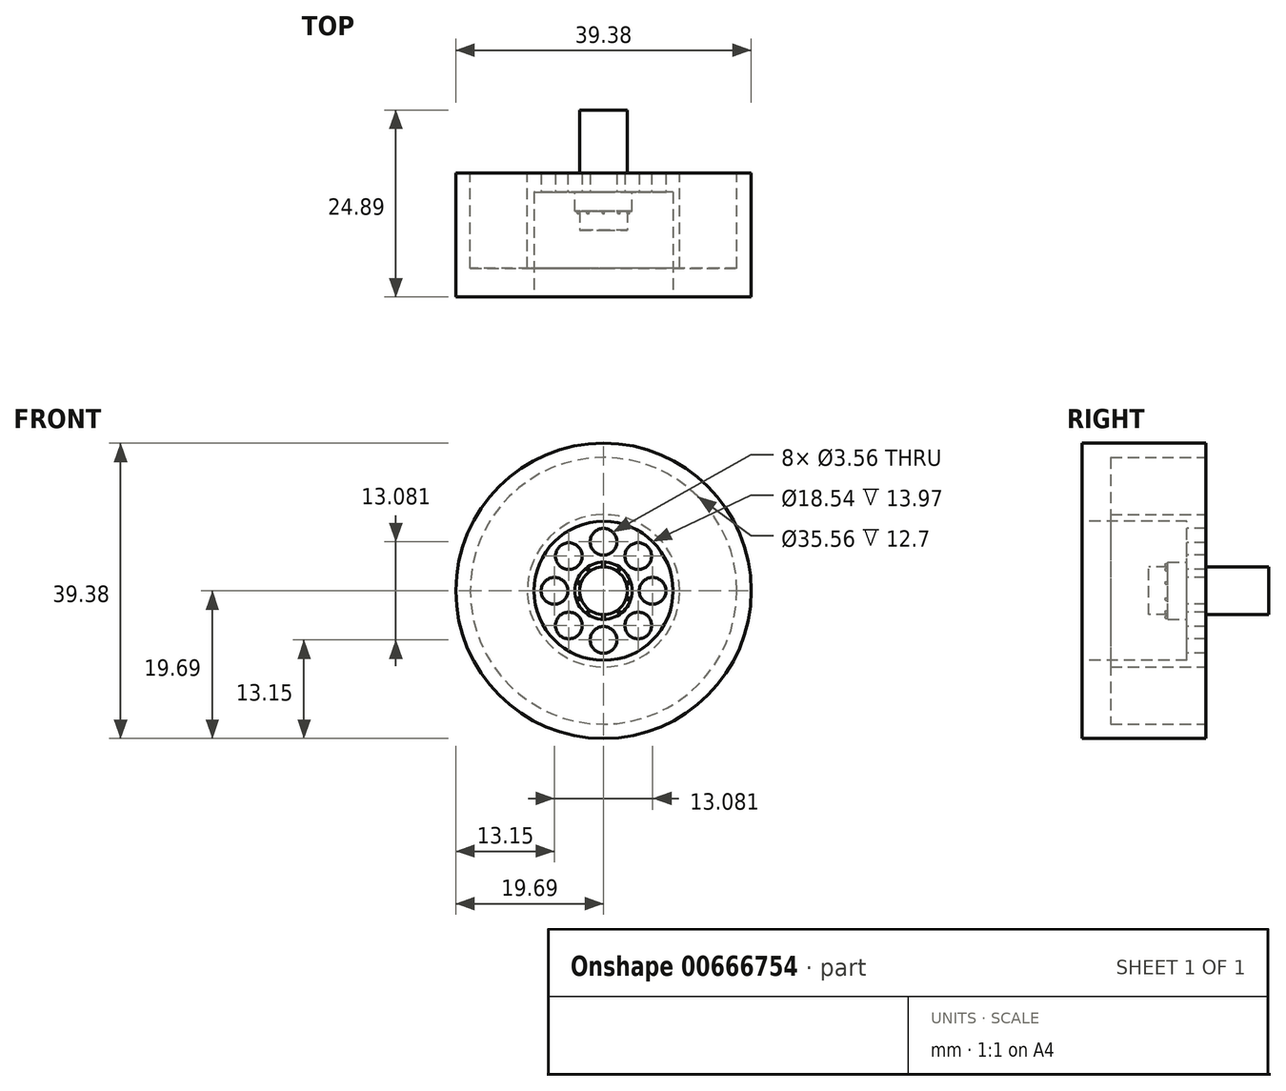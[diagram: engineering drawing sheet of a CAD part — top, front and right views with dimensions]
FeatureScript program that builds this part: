
annotation { "Feature Type Name" : "Feature", "Feature Type Description" : "" }
export const myFeature = defineFeature(function(context is Context, id is Id, definition is map)
    precondition{}
    {
        {
            var Q0;
            Q0=qCreatedBy(makeId("Front.planeOp"),FACE);
            var sketch = newSketch(context, id + "F0", { "sketchPlane" : qUnion([Q0])});
            skCircle(sketch, "E0", {"center": v(0, 0) * mm, "radius": 19.69 * mm});
            skCircle(sketch, "E1", {"center": v(0, 0) * mm, "radius": 8.9 * mm});
            skCircle(sketch, "E2", {"center": v(0, 0) * mm, "radius": 10.16 * mm});
            skSolve(sketch);
        }
        {
            var Q0;
            Q0=makeQuery(id+"F0.imprint","IMPRINT",FACE,{"disambiguationData":[TD([[makeQuery(id+"F0.imprint","IMPRINT",EDGE,{"derivedFrom":sQuery(id+"F0.wireOp",EDGE,"E0")}),1.0]])]});
            var Q1;
            Q1=makeQuery(id+"F0.imprint","IMPRINT",FACE,{"disambiguationData":[TD([[makeQuery(id+"F0.imprint","IMPRINT",EDGE,{"derivedFrom":sQuery(id+"F0.wireOp",EDGE,"E1")}),-1.0]])]});
            var Q2;
            Q2=makeQuery(id+"F0.imprint","IMPRINT",FACE,{"disambiguationData":[TD([[makeQuery(id+"F0.imprint","IMPRINT",EDGE,{"derivedFrom":sQuery(id+"F0.wireOp",EDGE,"E1")}),1.0]])]});
            extrude(context, id + "F1", {"entities" : qUnion([Q0, Q1, Q2]), "depth" : 24.9 * mm, "offsetDistance" : 25.4 * mm});
        }
        {
            var Q0;
            Q0=makeQuery(id+"F1.opExtrude","CAP_FACE",FACE,{"disambiguationData":[OSD([sQuery(id+"F0.wireOp",EDGE,"E0")])],"isStart":true});
            var sketch = newSketch(context, id + "F2", { "sketchPlane" : qUnion([Q0])});
            skCircle(sketch, "E3", {"center": v(0, 0) * mm, "radius": 3.18 * mm});
            skSolve(sketch);
        }
        {
            var Q0;
            Q0=makeQuery(id+"F2.imprint","IMPRINT",FACE,{"disambiguationData":[TD([[makeQuery(id+"F2.imprint","IMPRINT",EDGE,{"derivedFrom":sQuery(id+"F2.wireOp",EDGE,"E3")}),-1.0]])]});
            extrude(context, id + "F3", {"entities" : qUnion([Q0]), "operationType" : NewBodyOperationType.REMOVE, "oppositeDirection" : true, "depth" : 8.38 * mm, "offsetDistance" : 25.4 * mm});
        }
        {
            var Q0;
            Q0=makeQuery(id+"F1.opExtrude","CAP_FACE",FACE,{"disambiguationData":[OSD([sQuery(id+"F0.wireOp",EDGE,"E0")])],"isStart":false});
            var sketch = newSketch(context, id + "F4", { "sketchPlane" : qUnion([Q0])});
            skCircle(sketch, "E4", {"center": v(0, 0) * mm, "radius": 9.27 * mm});
            skSolve(sketch);
        }
        {
            var Q0;
            Q0=makeQuery(id+"F4.imprint","IMPRINT",FACE,{"disambiguationData":[TD([[makeQuery(id+"F4.imprint","IMPRINT",EDGE,{"derivedFrom":sQuery(id+"F4.wireOp",EDGE,"E4")}),1.0]])]});
            extrude(context, id + "F5", {"entities" : qUnion([Q0]), "operationType" : NewBodyOperationType.REMOVE, "oppositeDirection" : true, "depth" : 8.9 * mm, "offsetDistance" : 25.4 * mm});
        }
        {
            var Q0;
            Q0=makeQuery(id+"F5.boolean.opBoolean","COPY",FACE,{"derivedFrom":makeQuery(id+"F5.opExtrude","CAP_FACE",FACE,{"disambiguationData":[OSD([sQuery(id+"F4.wireOp",EDGE,"E4")])],"isStart":false})});
            var sketch = newSketch(context, id + "F6", { "sketchPlane" : qUnion([Q0])});
            skCircle(sketch, "E5", {"center": v(0, 0) * mm, "radius": 3.18 * mm});
            skSolve(sketch);
        }
        {
            var Q0;
            Q0=makeQuery(id+"F6.imprint","IMPRINT",FACE,{"disambiguationData":[TD([[makeQuery(id+"F6.imprint","IMPRINT",EDGE,{"derivedFrom":sQuery(id+"F6.wireOp",EDGE,"E5")}),-1.0]])]});
            extrude(context, id + "F7", {"entities" : qUnion([Q0]), "operationType" : NewBodyOperationType.REMOVE, "oppositeDirection" : true, "depth" : 5.08 * mm, "offsetDistance" : 25.4 * mm});
        }
        {
            var Q0;
            Q0=makeQuery(id+"F7.boolean.opBoolean","COPY",FACE,{"derivedFrom":makeQuery(id+"F7.opExtrude","CAP_FACE",FACE,{"disambiguationData":[OSD([sQuery(id+"F4.wireOp",EDGE,"E4"),sQuery(id+"F6.wireOp",EDGE,"E5")])],"isStart":false})});
            var sketch = newSketch(context, id + "F8", { "sketchPlane" : qUnion([Q0])});
            skCircle(sketch, "E6", {"center": v(0, 0) * mm, "radius": 3.81 * mm});
            skSolve(sketch);
        }
        {
            var Q0;
            Q0=makeQuery(id+"F8.imprint","IMPRINT",FACE,{"disambiguationData":[TD([[makeQuery(id+"F8.imprint","IMPRINT",EDGE,{"derivedFrom":sQuery(id+"F8.wireOp",EDGE,"E6")}),1.0]])]});
            extrude(context, id + "F9", {"entities" : qUnion([Q0]), "operationType" : NewBodyOperationType.ADD, "depth" : 2.54 * mm, "offsetDistance" : 25.4 * mm});
        }
        {
            var Q0;
            Q0=makeQuery(id+"F7.boolean.opBoolean","COPY",FACE,{"derivedFrom":makeQuery(id+"F7.opExtrude","CAP_FACE",FACE,{"disambiguationData":[OSD([sQuery(id+"F4.wireOp",EDGE,"E4"),sQuery(id+"F6.wireOp",EDGE,"E5")])],"isStart":false})});
            var sketch = newSketch(context, id + "F10", { "sketchPlane" : qUnion([Q0])});
            skLineSegment(sketch, "E7", {"start": v(0, 3.81) * mm, "end": v(0, 6.54) * mm});
            skCircle(sketch, "E8", {"center": v(0, 6.54) * mm, "radius": 1.78 * mm});
            skCircle(sketch, "E9.1.0", {"center": v(-4.62, 4.62) * mm, "radius": 1.78 * mm});
            skCircle(sketch, "E9.2.0", {"center": v(-6.54, 0) * mm, "radius": 1.78 * mm});
            skPoint(sketch, "E9.center", {"position": v(0, 0) * mm});
            skCircle(sketch, "E10.1.3.0", {"center": v(-4.62, -4.62) * mm, "radius": 1.78 * mm});
            skCircle(sketch, "E10.1.4.0", {"center": v(0, -6.54) * mm, "radius": 1.78 * mm});
            skCircle(sketch, "E10.1.5.0", {"center": v(4.62, -4.62) * mm, "radius": 1.78 * mm});
            skCircle(sketch, "E10.1.6.0", {"center": v(6.54, 0) * mm, "radius": 1.78 * mm});
            skCircle(sketch, "E10.1.7.0", {"center": v(4.62, 4.62) * mm, "radius": 1.78 * mm});
            skSolve(sketch);
        }
        {
            var Q0;
            Q0=makeQuery(id+"F10.imprint","IMPRINT",FACE,{"disambiguationData":[TD([[makeQuery(id+"F10.imprint","IMPRINT",EDGE,{"derivedFrom":sQuery(id+"F10.wireOp",EDGE,"E9.1.0")}),1.0]])]});
            var Q1;
            Q1=makeQuery(id+"F10.imprint","IMPRINT",FACE,{"disambiguationData":[TD([[makeQuery(id+"F10.imprint","IMPRINT",EDGE,{"derivedFrom":sQuery(id+"F10.wireOp",EDGE,"E8")}),1.0]])]});
            var Q2;
            Q2=makeQuery(id+"F10.imprint","IMPRINT",FACE,{"disambiguationData":[TD([[makeQuery(id+"F10.imprint","IMPRINT",EDGE,{"derivedFrom":sQuery(id+"F10.wireOp",EDGE,"E10.1.7.0")}),1.0]])]});
            var Q3;
            Q3=makeQuery(id+"F10.imprint","IMPRINT",FACE,{"disambiguationData":[TD([[makeQuery(id+"F10.imprint","IMPRINT",EDGE,{"derivedFrom":sQuery(id+"F10.wireOp",EDGE,"E10.1.6.0")}),1.0]])]});
            var Q4;
            Q4=makeQuery(id+"F10.imprint","IMPRINT",FACE,{"disambiguationData":[TD([[makeQuery(id+"F10.imprint","IMPRINT",EDGE,{"derivedFrom":sQuery(id+"F10.wireOp",EDGE,"E10.1.5.0")}),1.0]])]});
            var Q5;
            Q5=makeQuery(id+"F10.imprint","IMPRINT",FACE,{"disambiguationData":[TD([[makeQuery(id+"F10.imprint","IMPRINT",EDGE,{"derivedFrom":sQuery(id+"F10.wireOp",EDGE,"E10.1.4.0")}),1.0]])]});
            var Q6;
            Q6=makeQuery(id+"F10.imprint","IMPRINT",FACE,{"disambiguationData":[TD([[makeQuery(id+"F10.imprint","IMPRINT",EDGE,{"derivedFrom":sQuery(id+"F10.wireOp",EDGE,"E10.1.3.0")}),1.0]])]});
            var Q7;
            Q7=makeQuery(id+"F10.imprint","IMPRINT",FACE,{"disambiguationData":[TD([[makeQuery(id+"F10.imprint","IMPRINT",EDGE,{"derivedFrom":sQuery(id+"F10.wireOp",EDGE,"E9.2.0")}),1.0]])]});
            extrude(context, id + "F11", {"entities" : qUnion([Q0, Q1, Q2, Q3, Q4, Q5, Q6, Q7]), "operationType" : NewBodyOperationType.REMOVE, "oppositeDirection" : true, "depth" : 7.67 * mm, "offsetDistance" : 25.4 * mm});
        }
        {
            var Q0;
            Q0=makeQuery(id+"F9.opExtrude","CAP_FACE",FACE,{"disambiguationData":[OSD([sQuery(id+"F6.wireOp",EDGE,"E5"),sQuery(id+"F8.wireOp",EDGE,"E6")])],"isStart":false});
            var sketch = newSketch(context, id + "F12", { "sketchPlane" : qUnion([Q0])});
            skLineSegment(sketch, "E11", {"start": v(0, 3.18) * mm, "end": v(0, 3.5) * mm});
            skCircle(sketch, "E12", {"center": v(0, 3.5) * mm, "radius": 0.15 * mm});
            skCircle(sketch, "E13.1.0", {"center": v(-2.05, 2.83) * mm, "radius": 0.15 * mm});
            skCircle(sketch, "E13.2.0", {"center": v(-3.32, 1.08) * mm, "radius": 0.15 * mm});
            skCircle(sketch, "E13.3.0", {"center": v(-3.32, -1.08) * mm, "radius": 0.15 * mm});
            skCircle(sketch, "E13.4.0", {"center": v(-2.05, -2.83) * mm, "radius": 0.15 * mm});
            skCircle(sketch, "E13.5.0", {"center": v(0, -3.5) * mm, "radius": 0.15 * mm});
            skCircle(sketch, "E13.6.0", {"center": v(2.05, -2.83) * mm, "radius": 0.15 * mm});
            skCircle(sketch, "E13.7.0", {"center": v(3.32, -1.08) * mm, "radius": 0.15 * mm});
            skCircle(sketch, "E13.8.0", {"center": v(3.32, 1.08) * mm, "radius": 0.15 * mm});
            skCircle(sketch, "E13.9.0", {"center": v(2.05, 2.83) * mm, "radius": 0.15 * mm});
            skPoint(sketch, "E13.center", {"position": v(0, 0) * mm});
            skSolve(sketch);
        }
        {
            var Q0;
            Q0=makeQuery(id+"F12.imprint","IMPRINT",FACE,{"disambiguationData":[TD([[makeQuery(id+"F12.imprint","IMPRINT",EDGE,{"derivedFrom":sQuery(id+"F12.wireOp",EDGE,"E12")}),1.0]])]});
            var Q1;
            Q1=makeQuery(id+"F12.imprint","IMPRINT",FACE,{"disambiguationData":[TD([[makeQuery(id+"F12.imprint","IMPRINT",EDGE,{"derivedFrom":sQuery(id+"F12.wireOp",EDGE,"E13.9.0")}),1.0]])]});
            var Q2;
            Q2=makeQuery(id+"F12.imprint","IMPRINT",FACE,{"disambiguationData":[TD([[makeQuery(id+"F12.imprint","IMPRINT",EDGE,{"derivedFrom":sQuery(id+"F12.wireOp",EDGE,"E13.8.0")}),1.0]])]});
            var Q3;
            Q3=makeQuery(id+"F12.imprint","IMPRINT",FACE,{"disambiguationData":[TD([[makeQuery(id+"F12.imprint","IMPRINT",EDGE,{"derivedFrom":sQuery(id+"F12.wireOp",EDGE,"E13.7.0")}),1.0]])]});
            var Q4;
            Q4=makeQuery(id+"F12.imprint","IMPRINT",FACE,{"disambiguationData":[TD([[makeQuery(id+"F12.imprint","IMPRINT",EDGE,{"derivedFrom":sQuery(id+"F12.wireOp",EDGE,"E13.6.0")}),1.0]])]});
            var Q5;
            Q5=makeQuery(id+"F12.imprint","IMPRINT",FACE,{"disambiguationData":[TD([[makeQuery(id+"F12.imprint","IMPRINT",EDGE,{"derivedFrom":sQuery(id+"F12.wireOp",EDGE,"E13.5.0")}),1.0]])]});
            var Q6;
            Q6=makeQuery(id+"F12.imprint","IMPRINT",FACE,{"disambiguationData":[TD([[makeQuery(id+"F12.imprint","IMPRINT",EDGE,{"derivedFrom":sQuery(id+"F12.wireOp",EDGE,"E13.4.0")}),1.0]])]});
            var Q7;
            Q7=makeQuery(id+"F12.imprint","IMPRINT",FACE,{"disambiguationData":[TD([[makeQuery(id+"F12.imprint","IMPRINT",EDGE,{"derivedFrom":sQuery(id+"F12.wireOp",EDGE,"E13.3.0")}),1.0]])]});
            var Q8;
            Q8=makeQuery(id+"F12.imprint","IMPRINT",FACE,{"disambiguationData":[TD([[makeQuery(id+"F12.imprint","IMPRINT",EDGE,{"derivedFrom":sQuery(id+"F12.wireOp",EDGE,"E13.2.0")}),1.0]])]});
            var Q9;
            Q9=makeQuery(id+"F12.imprint","IMPRINT",FACE,{"disambiguationData":[TD([[makeQuery(id+"F12.imprint","IMPRINT",EDGE,{"derivedFrom":sQuery(id+"F12.wireOp",EDGE,"E13.1.0")}),1.0]])]});
            extrude(context, id + "F13", {"entities" : qUnion([Q0, Q1, Q2, Q3, Q4, Q5, Q6, Q7, Q8, Q9]), "operationType" : NewBodyOperationType.ADD, "depth" : 0.32 * mm, "offsetDistance" : 25.4 * mm});
        }
        {
            var Q0;
            Q0=makeQuery(id+"F3.boolean.opBoolean","COPY",FACE,{"derivedFrom":makeQuery(id+"F3.opExtrude","CAP_FACE",FACE,{"disambiguationData":[OSD([sQuery(id+"F0.wireOp",EDGE,"E0"),sQuery(id+"F2.wireOp",EDGE,"E3")])],"isStart":false})});
            var sketch = newSketch(context, id + "F14", { "sketchPlane" : qUnion([Q0])});
            skCircle(sketch, "E14", {"center": v(0, 0) * mm, "radius": 17.78 * mm});
            skSolve(sketch);
        }
        {
            var Q0;
            Q0=makeQuery(id+"F14.imprint","IMPRINT",FACE,{"disambiguationData":[TD([[makeQuery(id+"F14.imprint","IMPRINT",EDGE,{"derivedFrom":sQuery(id+"F14.wireOp",EDGE,"E14")}),1.0]])]});
            var sketch = newSketch(context, id + "F15", { "sketchPlane" : qUnion([Q0])});
            skCircle(sketch, "E15", {"center": v(0, 0) * mm, "radius": 10.16 * mm});
            skSolve(sketch);
        }
        {
            var Q0;
            Q0=makeQuery(id+"F15.imprint","IMPRINT",FACE,{"disambiguationData":[TD([[makeQuery(id+"F15.imprint","IMPRINT",EDGE,{"derivedFrom":sQuery(id+"F15.wireOp",EDGE,"E15")}),-1.0]])]});
            extrude(context, id + "F16", {"entities" : qUnion([Q0]), "operationType" : NewBodyOperationType.REMOVE, "oppositeDirection" : true, "depth" : 12.7 * mm, "offsetDistance" : 25.4 * mm});
        }
    });
